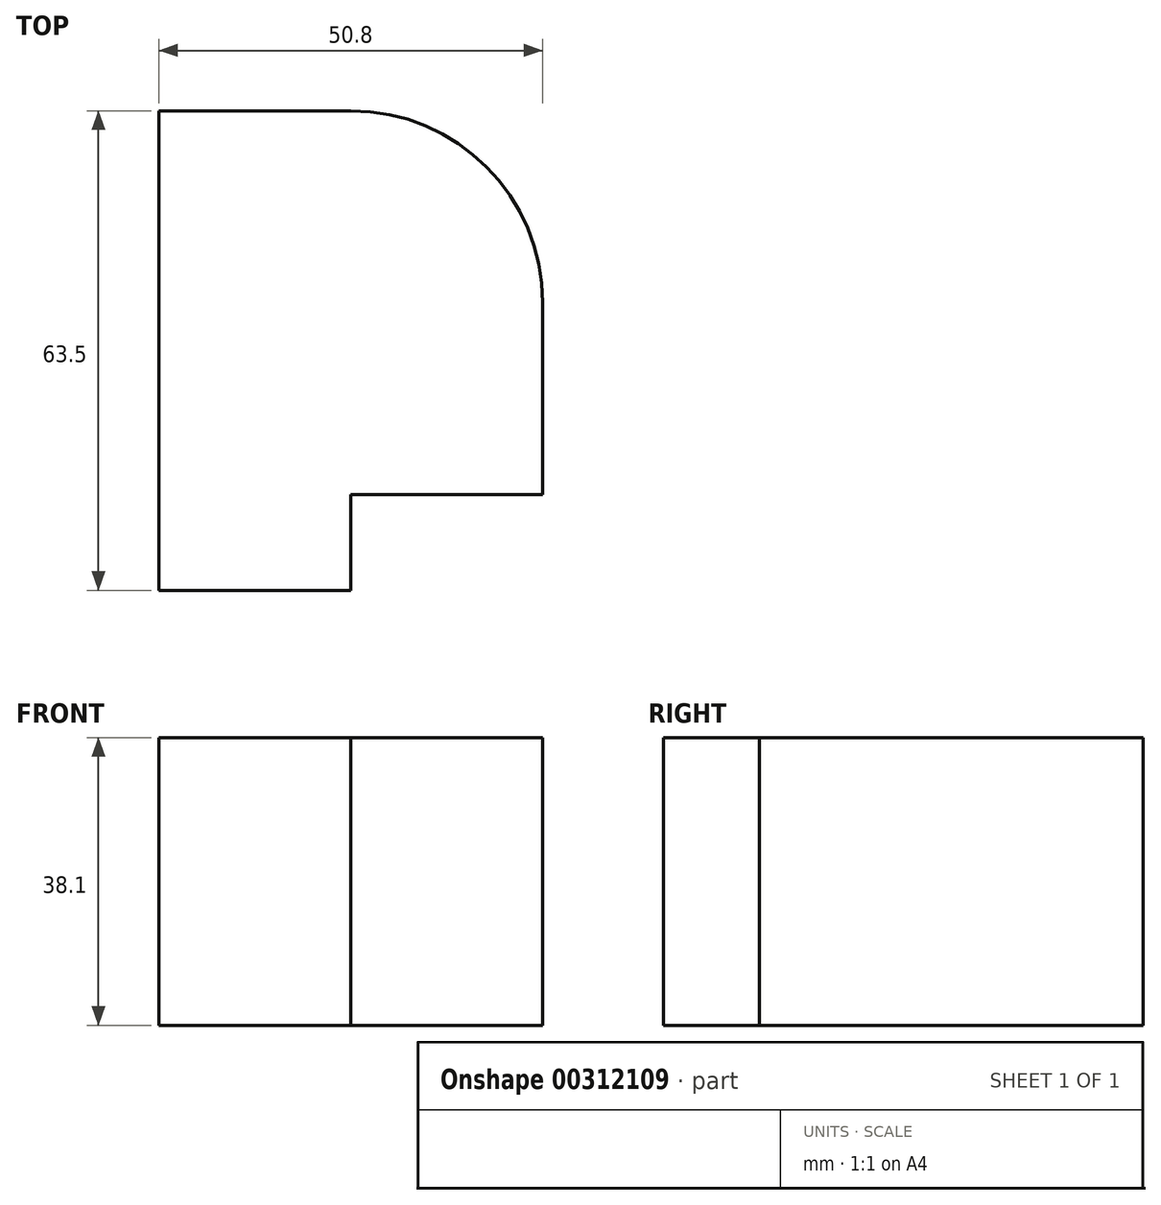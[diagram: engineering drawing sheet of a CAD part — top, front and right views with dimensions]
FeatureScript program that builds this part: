
annotation { "Feature Type Name" : "Feature", "Feature Type Description" : "" }
export const myFeature = defineFeature(function(context is Context, id is Id, definition is map)
    precondition{}
    {
        {
            var Q0;
            Q0=qCreatedBy(makeId("Top.planeOp"),FACE);
            var sketch = newSketch(context, id + "F0", { "sketchPlane" : qUnion([Q0])});
            skLineSegment(sketch, "E0.bottom", {"start": v(0, 0) * mm, "end": v(50.8, 0) * mm});
            skLineSegment(sketch, "E0.top", {"start": v(0, 50.8) * mm, "end": v(25.4, 50.8) * mm});
            skLineSegment(sketch, "E0.left", {"start": v(0, 0) * mm, "end": v(0, 50.8) * mm});
            skLineSegment(sketch, "E0.right", {"start": v(50.8, 0) * mm, "end": v(50.8, 25.4) * mm});
            skLineSegment(sketch, "E1.bottom", {"start": v(25.4, -12.7) * mm, "end": v(0, -12.7) * mm});
            skLineSegment(sketch, "E1.top", {"start": v(25.4, 0) * mm, "end": v(0, 0) * mm});
            skLineSegment(sketch, "E1.left", {"start": v(25.4, -12.7) * mm, "end": v(25.4, 0) * mm});
            skLineSegment(sketch, "E1.right", {"start": v(0, -12.7) * mm, "end": v(0, 0) * mm});
            skPoint(sketch, "E2.visualSharp", {"position": v(50.8, 50.8) * mm});
            skArc(sketch, "E2.filletArc", {"start": v(50.8, 25.4) * mm, "mid": v(43.36, 43.36) * mm, "end": v(25.4, 50.8) * mm});
            skSolve(sketch);
        }
        {
            var Q0;
            Q0=makeQuery(id+"F0.imprint","IMPRINT",FACE,{"disambiguationData":[TD([[makeQuery(id+"F0.imprint","IMPRINT",EDGE,{"derivedFrom":sQuery(id+"F0.wireOp",EDGE,"E0.bottom")}),1.0]])]});
            var Q1;
            Q1=makeQuery(id+"F0.imprint","IMPRINT",FACE,{"disambiguationData":[TD([[makeQuery(id+"F0.imprint","IMPRINT",EDGE,{"derivedFrom":sQuery(id+"F0.wireOp",EDGE,"E1.bottom")}),-1.0]])]});
            extrude(context, id + "F1", {"entities" : qUnion([Q0, Q1]), "depth" : 38.1 * mm});
        }
    });
